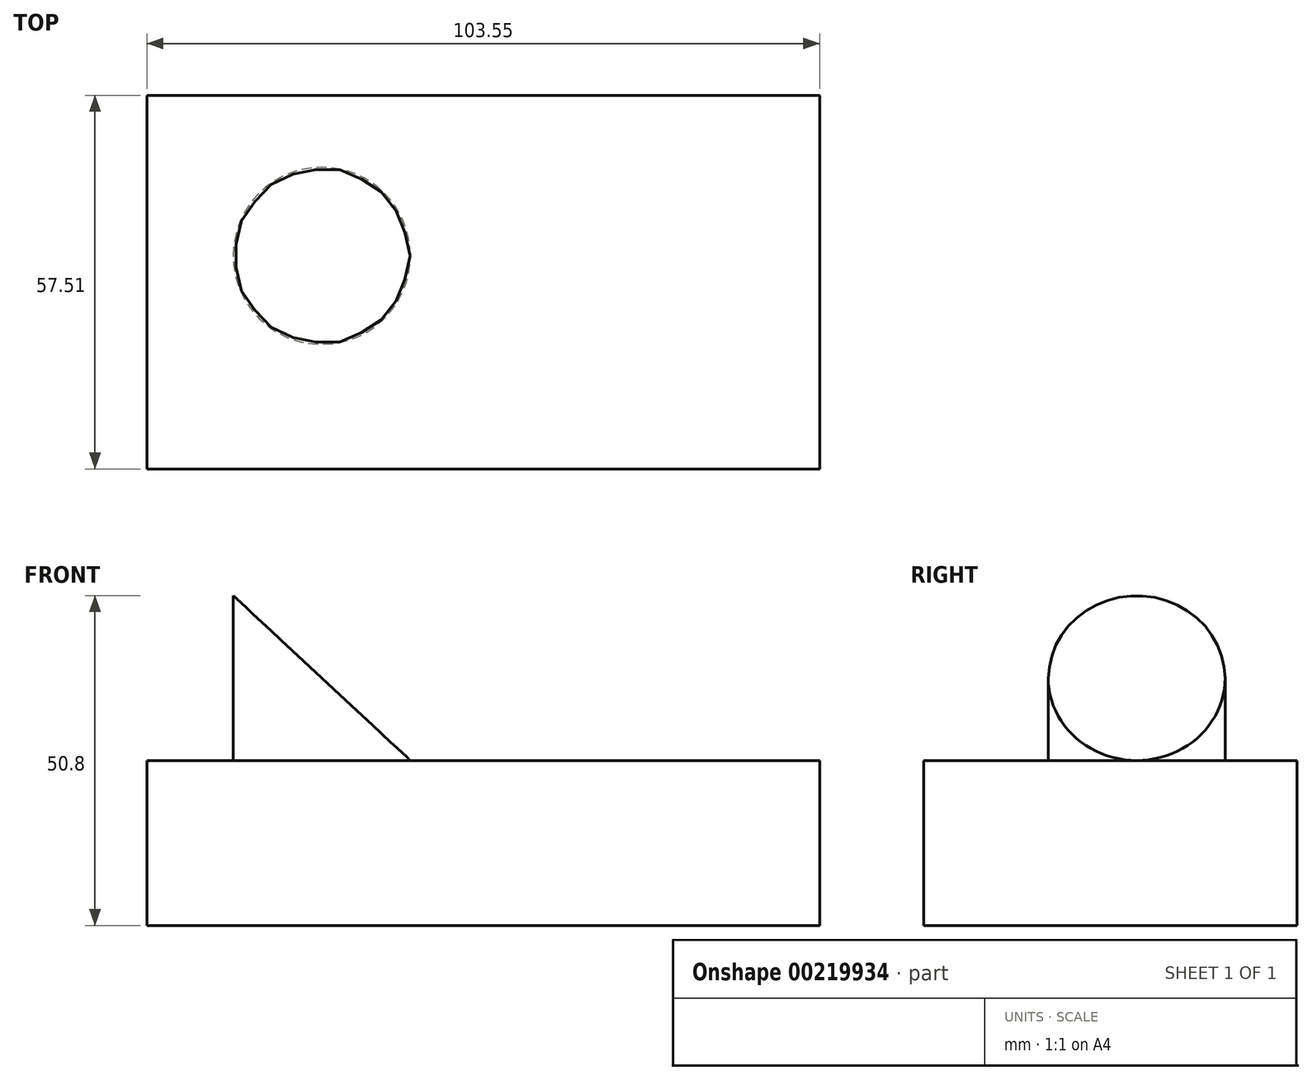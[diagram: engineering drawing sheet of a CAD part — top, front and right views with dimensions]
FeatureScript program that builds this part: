
annotation { "Feature Type Name" : "Feature", "Feature Type Description" : "" }
export const myFeature = defineFeature(function(context is Context, id is Id, definition is map)
    precondition{}
    {
        {
            var Q0;
            Q0=qCreatedBy(makeId("Top.planeOp"),FACE);
            var sketch = newSketch(context, id + "F0", { "sketchPlane" : qUnion([Q0])});
            skLineSegment(sketch, "E0.bottom", {"start": v(-103.55, 11.96) * mm, "end": v(0, 11.96) * mm});
            skLineSegment(sketch, "E0.top", {"start": v(-103.55, -45.55) * mm, "end": v(0, -45.55) * mm});
            skLineSegment(sketch, "E0.left", {"start": v(-103.55, 11.96) * mm, "end": v(-103.55, -45.55) * mm});
            skLineSegment(sketch, "E0.right", {"start": v(0, 11.96) * mm, "end": v(0, -45.55) * mm});
            skSolve(sketch);
        }
        {
            var Q0;
            Q0=makeQuery(id+"F0.imprint","IMPRINT",FACE,{"disambiguationData":[TD([[makeQuery(id+"F0.imprint","IMPRINT",EDGE,{"derivedFrom":sQuery(id+"F0.wireOp",EDGE,"E0.bottom")}),-1.0]])]});
            extrude(context, id + "F1", {"entities" : qUnion([Q0]), "depth" : 25.4 * mm});
        }
        {
            var Q0;
            Q0=makeQuery(id+"F1.opExtrude","CAP_FACE",FACE,{"disambiguationData":[OSD([sQuery(id+"F0.wireOp",EDGE,"E0.bottom"),sQuery(id+"F0.wireOp",EDGE,"E0.top"),sQuery(id+"F0.wireOp",EDGE,"E0.left"),sQuery(id+"F0.wireOp",EDGE,"E0.right")])],"isStart":false});
            var sketch = newSketch(context, id + "F2", { "sketchPlane" : qUnion([Q0])});
            skCircle(sketch, "E1", {"center": v(-76.64, -12.75) * mm, "radius": 13.62 * mm});
            skSolve(sketch);
        }
        {
            var Q0;
            Q0=makeQuery(id+"F2.imprint","IMPRINT",FACE,{"disambiguationData":[TD([[makeQuery(id+"F2.imprint","IMPRINT",EDGE,{"derivedFrom":sQuery(id+"F2.wireOp",EDGE,"E1")}),1.0]])]});
            extrude(context, id + "F3", {"entities" : qUnion([Q0]), "operationType" : NewBodyOperationType.ADD, "depth" : 25.4 * mm});
        }
        {
            var Q0;
            Q0=makeQuery(id+"F1.opExtrude","SWEPT_FACE",FACE,{"disambiguationData":[OSD([sQuery(id+"F0.wireOp",EDGE,"E0.top")])]});
            var sketch = newSketch(context, id + "F4", { "sketchPlane" : qUnion([Q0])});
            skSolve(sketch);
        }
        {
            var Q0;
            {var subQ0=sQuery(id+"F0.wireOp",EDGE,"E0.top");Q0=makeQuery(id+"F4.imprint","IMPRINT",FACE,{"disambiguationData":[TD([[makeQuery(id+"F4.imprint","IMPRINT",EDGE,{"derivedFrom":makeQuery(id+"F1.opExtrude","CAP_EDGE",EDGE,{"disambiguationData":[OSD([subQ0])],"isStart":true})}),1.0]])]});}
            var sketch = newSketch(context, id + "F5", { "sketchPlane" : qUnion([Q0])});
            skLineSegment(sketch, "E2.0", {"start": v(-90.27, 50.8) * mm, "end": v(-63.02, 50.8) * mm});
            skLineSegment(sketch, "E3", {"start": v(-63.02, 50.8) * mm, "end": v(-63.02, 25.4) * mm});
            skLineSegment(sketch, "E4", {"start": v(-90.27, 50.8) * mm, "end": v(-63.02, 25.4) * mm});
            skSolve(sketch);
        }
        {
            var Q0;
            Q0 = qSketchRegion(id + "F5", true);
            extrude(context, id + "F6", {"entities" : qUnion([Q0]), "operationType" : NewBodyOperationType.REMOVE, "endBound" : BoundingType.THROUGH_ALL, "oppositeDirection" : true, "depth" : 25.4 * mm});
        }
    });
